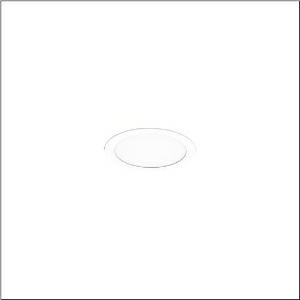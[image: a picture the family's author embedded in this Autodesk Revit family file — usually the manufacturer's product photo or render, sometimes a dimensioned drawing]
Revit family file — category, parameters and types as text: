
# Revit family: lunis_21_m_51db16mc91c
name_source: partatom
category: Lighting Fixtures
units: mm (PartAtom-declared; Revit-internal decimal feet)

## family parameters
Cut with Voids When Loaded = No
Host = Face
Light Source = No
Part Type = Normal
Room Calculation Point = No
Round Connector Dimension = Use Diameter
Shared = No

## types (1)
- --- (1 x LED, 3280 lm, 25.5 W, 6500K)
    Apparent Load = 26 VA
    CIE Flux Codes = 50 80 96 100 100
    Color Rendering = 80
    Color Temperature = 6500K
    Default Elevation = 1800 mm
    Description = Lunis 21,  M, downlight, light control with lens, of PMMA, optical cover: cover panel, of PC, opal, light emission: direct distribution, LED rated luminous flux: 1.490lm, light colour: 830/840/865, with terminal, 3-pole, mains connection: 220..240V, AC/DC, 0/50..60Hz, housing, round, of diecast aluminium, traffic white (RAL 9016), diameter: 115mm, clamping range: 1..40mm, protection rating (complete): IP20, protection rating (on room side): IP54, insulation class (complete): insulation class II (safety insulation), certification: CE, impact resistance: IK03, packaging unit: 1 piece
    Height = 0 mm  [stored 0 ft]
    Lamp = 1 x LED
    Lamp Light Flux = 3280 lm
    Lamp Power = 25.5 W
    Lamp count = 1
    Length = 115 mm
    Luminous efficacy = 129 lm/W
    Manufacturer = Siteco
    ModVariant = No
    Model = 51DB16MC91C
    Mounting Place = Ceiling
    Mounting Type = Recessed
    Number of Poles = 1
    OnlyDefault = Yes
    Power Factor = 1
    Product Name = Lunis 21 M
    Product group = downlight
    ProductGroupID = 401
    Protection Class = Protection class II
    Protection Degree = IP 20
    RLX_Detail_Level = 1
    RLX_Emergency_Light_Flux = 0 lm
    RLX_Emergency_Type = 0
    RLX_Emergency_Type_DB = No
    RlxData = <blob elided: 13497 chars, md5=c0f14deb>
    Socket = socket
    Standby Power = 0 W
    System Light Flux = 3280 lm
    System Power = 26 W
    Type Comments = individual setting: colour temperature 6500K, luminous flux: 100 % | (ON | ON | OFF | OFF) | 700 mA
    Type Image = l_1290848.jpg
    URL = http://relux.com
    VarID = @adj_038507
    Voltage = 0 V
    Weight = 0.00 kg
    Width = 0 mm  [stored 0 ft]

note: [stored X ft] marks values corroborated as IEEE doubles in the binary element streams (Revit-internal decimal feet)

## geometry (parser evidence)
native form markers: Sweep x10
no freeform markers — native parametric forms only
